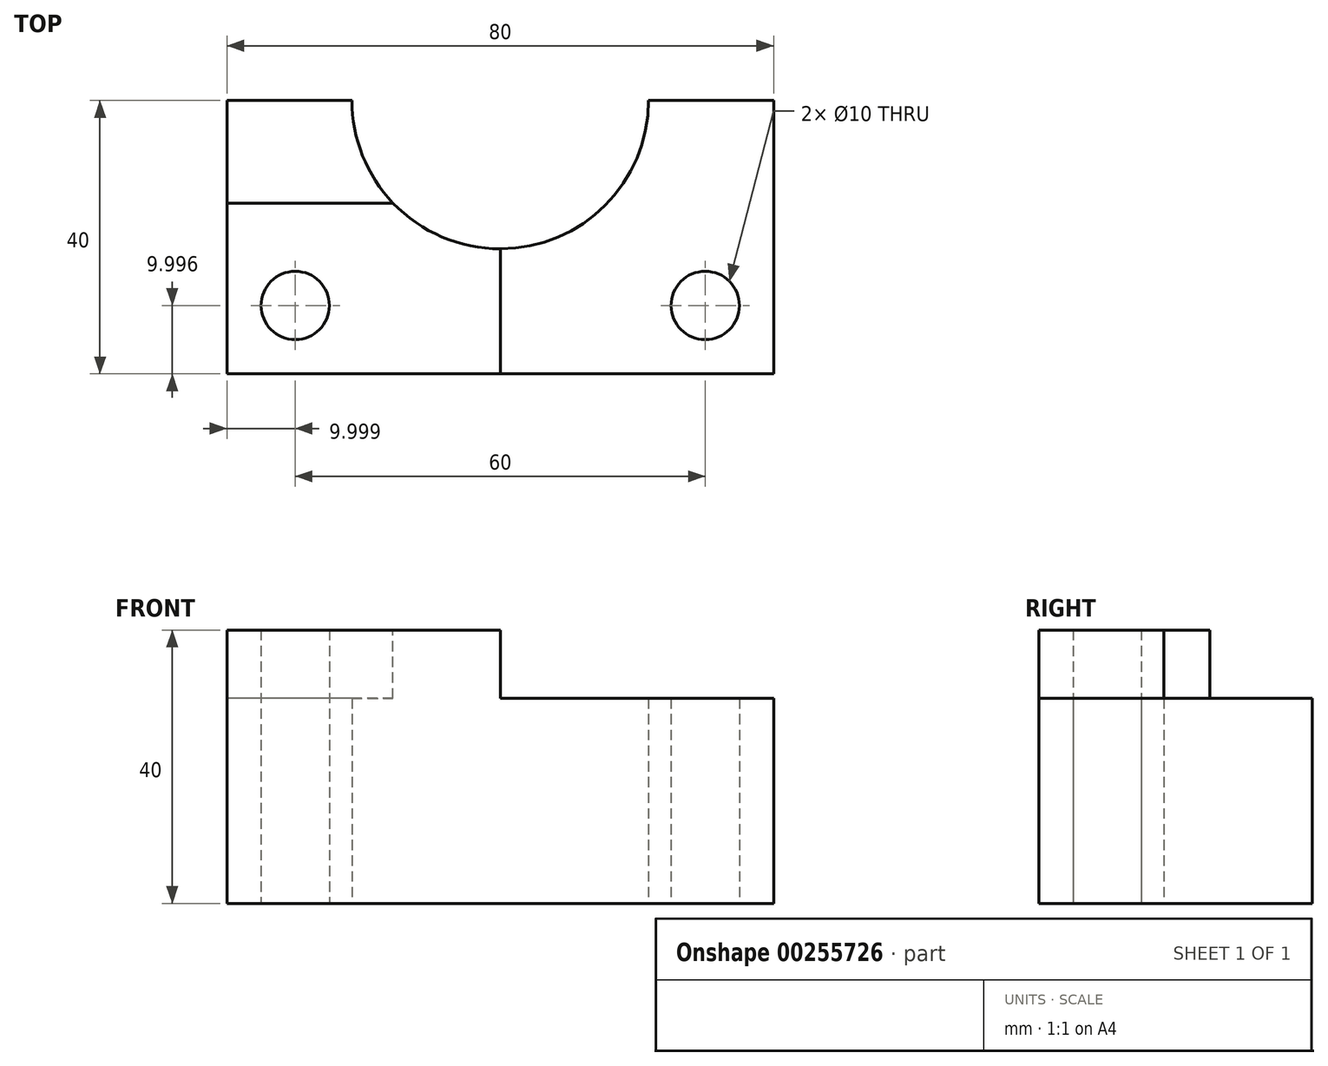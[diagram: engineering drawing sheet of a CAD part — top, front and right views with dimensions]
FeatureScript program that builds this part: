
annotation { "Feature Type Name" : "Feature", "Feature Type Description" : "" }
export const myFeature = defineFeature(function(context is Context, id is Id, definition is map)
    precondition{}
    {
        {
            var Q0;
            Q0=qCreatedBy(makeId("Top.planeOp"),FACE);
            var sketch = newSketch(context, id + "F0", { "sketchPlane" : qUnion([Q0])});
            skLineSegment(sketch, "E0.bottom", {"start": v(-4.02, -2.3) * mm, "end": v(-84.02, -2.3) * mm});
            skLineSegment(sketch, "E0.top", {"start": v(-4.02, 37.7) * mm, "end": v(-22.31, 37.7) * mm});
            skLineSegment(sketch, "E0.left", {"start": v(-4.02, -2.3) * mm, "end": v(-4.02, 37.7) * mm});
            skLineSegment(sketch, "E0.right", {"start": v(-84.02, -2.3) * mm, "end": v(-84.02, 37.7) * mm});
            skPoint(sketch, "E0.middle", {"position": v(-44.02, 17.7) * mm});
            skArc(sketch, "E1", {"start": v(-65.73, 37.7) * mm, "mid": v(-44.02, 15.99) * mm, "end": v(-22.31, 37.7) * mm});
            skCircle(sketch, "E2", {"center": v(-74.02, 7.7) * mm, "radius": 5 * mm});
            skCircle(sketch, "E3", {"center": v(-14.02, 7.7) * mm, "radius": 5 * mm});
            skLineSegment(sketch, "E4.trimOffspring", {"start": v(-65.73, 37.7) * mm, "end": v(-84.02, 37.7) * mm});
            skSolve(sketch);
        }
        {
            var Q0;
            Q0=makeQuery(id+"F0.imprint","IMPRINT",FACE,{"disambiguationData":[TD([[makeQuery(id+"F0.imprint","IMPRINT",EDGE,{"derivedFrom":sQuery(id+"F0.wireOp",EDGE,"E0.bottom")}),-1.0]])]});
            extrude(context, id + "F1", {"entities" : qUnion([Q0]), "depth" : 40 * mm});
        }
        {
            var Q0;
            Q0=makeQuery(id+"F1.opExtrude","CAP_FACE",FACE,{"disambiguationData":[OSD([sQuery(id+"F0.wireOp",EDGE,"E0.bottom"),sQuery(id+"F0.wireOp",EDGE,"E0.top"),sQuery(id+"F0.wireOp",EDGE,"E0.left"),sQuery(id+"F0.wireOp",EDGE,"E0.right"),sQuery(id+"F0.wireOp",EDGE,"E1"),sQuery(id+"F0.wireOp",EDGE,"E2"),sQuery(id+"F0.wireOp",EDGE,"E3"),sQuery(id+"F0.wireOp",EDGE,"E4.trimOffspring")])],"isStart":false});
            var sketch = newSketch(context, id + "F2", { "sketchPlane" : qUnion([Q0])});
            skLineSegment(sketch, "E5.bottom", {"start": v(-57.13, 22.7) * mm, "end": v(-123.54, 22.7) * mm});
            skLineSegment(sketch, "E5.top", {"start": v(-57.13, 55.05) * mm, "end": v(-123.54, 55.05) * mm});
            skLineSegment(sketch, "E5.left", {"start": v(-57.13, 22.7) * mm, "end": v(-57.13, 55.05) * mm});
            skLineSegment(sketch, "E5.right", {"start": v(-123.54, 22.7) * mm, "end": v(-123.54, 55.05) * mm});
            skPoint(sketch, "E5.middle", {"position": v(-90.34, 38.87) * mm});
            skPoint(sketch, "E6.firstSnap0", {"position": v(-44.02, 15.99) * mm});
            skLineSegment(sketch, "E6.bottom", {"start": v(-44.02, 47.07) * mm, "end": v(4.34, 47.07) * mm});
            skLineSegment(sketch, "E6.top", {"start": v(-44.02, -8.61) * mm, "end": v(4.34, -8.61) * mm});
            skLineSegment(sketch, "E6.left", {"start": v(-44.02, 47.07) * mm, "end": v(-44.02, -8.61) * mm});
            skLineSegment(sketch, "E6.right", {"start": v(4.34, 47.07) * mm, "end": v(4.34, -8.61) * mm});
            skSolve(sketch);
        }
        {
            var Q0;
            {var subQ5=makeQuery(id+"F1.opExtrude","CAP_EDGE",EDGE,{"disambiguationData":[OSD([sQuery(id+"F0.wireOp",EDGE,"E4.trimOffspring")])],"isStart":false});Q0=makeQuery(id+"F2.imprint","IMPRINT",FACE,{"disambiguationData":[TD([[makeQuery(id+"F2.imprint","IMPRINT",EDGE,{"derivedFrom":subQ5}),1.0]])]});}
            var Q1;
            {var subQ4=makeQuery(id+"F1.opExtrude","CAP_EDGE",EDGE,{"disambiguationData":[OSD([sQuery(id+"F0.wireOp",EDGE,"E0.top")])],"isStart":false});Q1=makeQuery(id+"F2.imprint","IMPRINT",FACE,{"disambiguationData":[TD([[makeQuery(id+"F2.imprint","IMPRINT",EDGE,{"derivedFrom":subQ4}),1.0]])]});}
            extrude(context, id + "F3", {"entities" : qUnion([Q0, Q1]), "operationType" : NewBodyOperationType.REMOVE, "oppositeDirection" : true, "depth" : 10 * mm});
        }
    });
